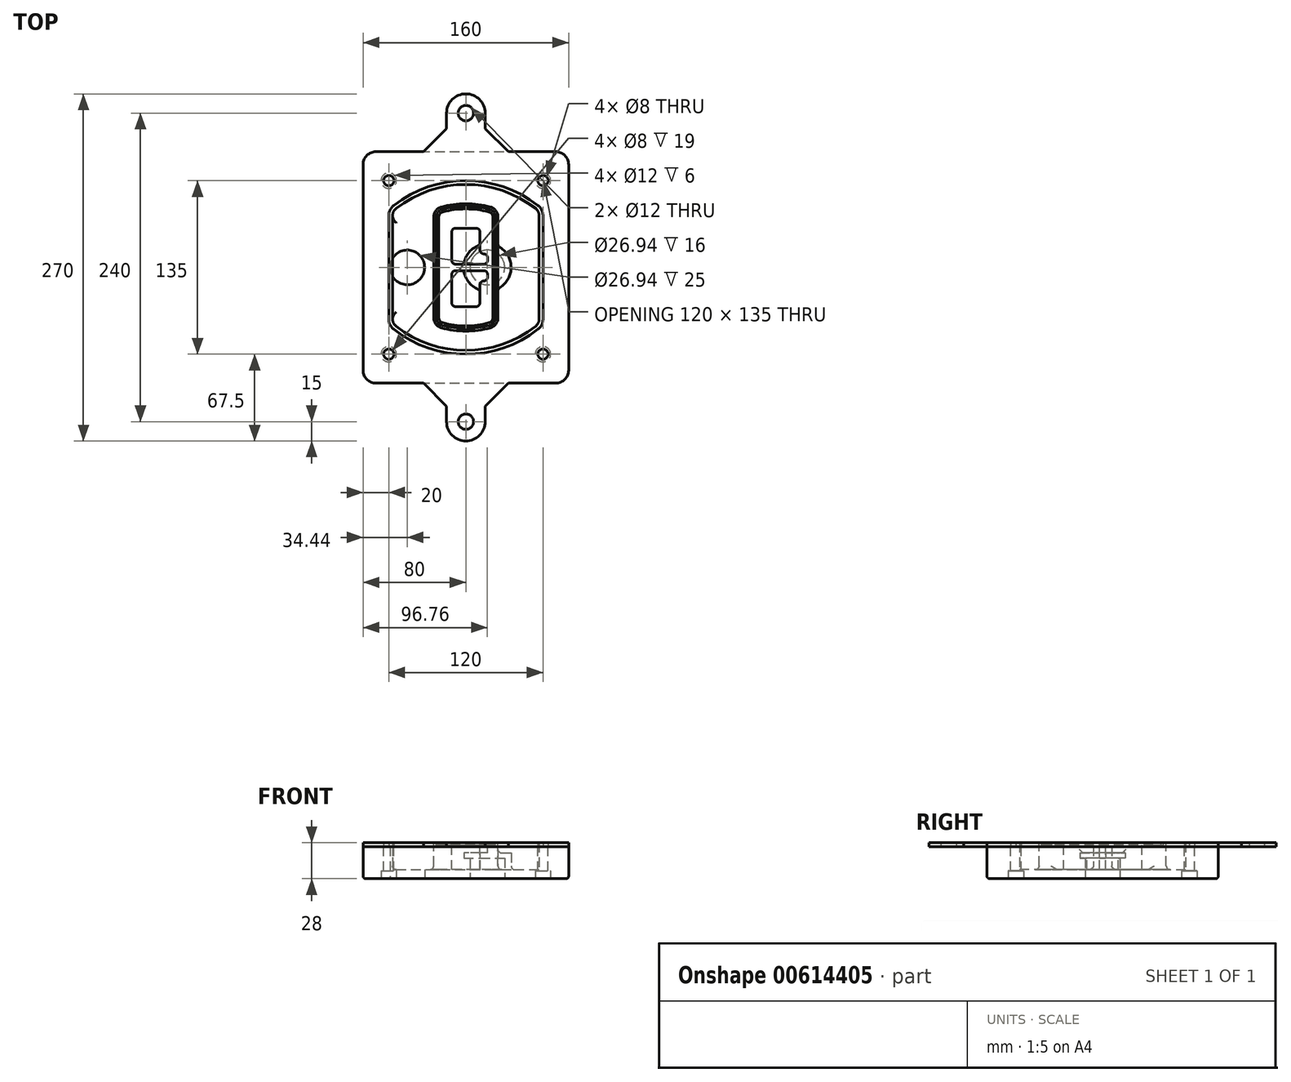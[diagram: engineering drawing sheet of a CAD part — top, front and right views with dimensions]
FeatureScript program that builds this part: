
annotation { "Feature Type Name" : "Feature", "Feature Type Description" : "" }
export const myFeature = defineFeature(function(context is Context, id is Id, definition is map)
    precondition{}
    {
        {
            var Q0;
            Q0=qCreatedBy(makeId("Top.planeOp"),FACE);
            var sketch = newSketch(context, id + "F0", { "sketchPlane" : qUnion([Q0])});
            skPoint(sketch, "E0.rect.middle", {"position": v(0, 0) * mm});
            skLineSegment(sketch, "E1.bottom", {"start": v(-70, -90) * mm, "end": v(70, -90) * mm});
            skLineSegment(sketch, "E1.top", {"start": v(-70, 90) * mm, "end": v(70, 90) * mm});
            skLineSegment(sketch, "E1.left", {"start": v(-80, -80) * mm, "end": v(-80, 80) * mm});
            skLineSegment(sketch, "E1.right", {"start": v(80, -80) * mm, "end": v(80, 80) * mm});
            skLineSegment(sketch, "E2", {"start": v(-80, 90) * mm, "end": v(80, -90) * mm, "construction": true});
            skLineSegment(sketch, "E3", {"start": v(80, 90) * mm, "end": v(-80, -90) * mm, "construction": true});
            skCircle(sketch, "E4", {"center": v(-60, 67.5) * mm, "radius": 4 * mm});
            skCircle(sketch, "E5", {"center": v(60, 67.5) * mm, "radius": 4 * mm});
            skCircle(sketch, "E6", {"center": v(60, -67.5) * mm, "radius": 4 * mm});
            skCircle(sketch, "E7", {"center": v(-60, -67.5) * mm, "radius": 4 * mm});
            skLineSegment(sketch, "E8", {"start": v(-60, 67.5) * mm, "end": v(60, 67.5) * mm, "construction": true});
            skLineSegment(sketch, "E9", {"start": v(60, 67.5) * mm, "end": v(60, -67.5) * mm, "construction": true});
            skLineSegment(sketch, "E10", {"start": v(60, -67.5) * mm, "end": v(-60, -67.5) * mm, "construction": true});
            skLineSegment(sketch, "E11", {"start": v(-60, -67.5) * mm, "end": v(-60, 67.5) * mm, "construction": true});
            skLineSegment(sketch, "E12", {"start": v(-60, 40.3) * mm, "end": v(-60, -40.3) * mm});
            skLineSegment(sketch, "E13", {"start": v(60, 40.3) * mm, "end": v(60, -40.3) * mm});
            skArc(sketch, "E14", {"start": v(56.15, 48.18) * mm, "mid": v(0, 67.5) * mm, "end": v(-56.15, 48.18) * mm});
            skArc(sketch, "E15", {"start": v(-56.15, -48.18) * mm, "mid": v(0, -67.5) * mm, "end": v(56.15, -48.18) * mm});
            skLineSegment(sketch, "E16", {"start": v(-60, 0) * mm, "end": v(60, 0) * mm, "construction": true});
            skPoint(sketch, "E17.visualSharp", {"position": v(-60, -45) * mm});
            skArc(sketch, "E17.filletArc", {"start": v(-60, -40.3) * mm, "mid": v(-58.99, -44.68) * mm, "end": v(-56.15, -48.18) * mm});
            skPoint(sketch, "E18.visualSharp", {"position": v(-60, 45) * mm});
            skArc(sketch, "E18.filletArc", {"start": v(-56.15, 48.18) * mm, "mid": v(-58.99, 44.68) * mm, "end": v(-60, 40.3) * mm});
            skPoint(sketch, "E19.visualSharp", {"position": v(60, 45) * mm});
            skArc(sketch, "E19.filletArc", {"start": v(60, 40.3) * mm, "mid": v(58.99, 44.68) * mm, "end": v(56.15, 48.18) * mm});
            skPoint(sketch, "E20.visualSharp", {"position": v(60, -45) * mm});
            skArc(sketch, "E20.filletArc", {"start": v(56.15, -48.18) * mm, "mid": v(58.99, -44.68) * mm, "end": v(60, -40.3) * mm});
            skPoint(sketch, "E21.visualSharp", {"position": v(-80, 90) * mm});
            skArc(sketch, "E21.filletArc", {"start": v(-70, 90) * mm, "mid": v(-77.07, 87.07) * mm, "end": v(-80, 80) * mm});
            skPoint(sketch, "E22.visualSharp", {"position": v(80, 90) * mm});
            skArc(sketch, "E22.filletArc", {"start": v(80, 80) * mm, "mid": v(77.07, 87.07) * mm, "end": v(70, 90) * mm});
            skPoint(sketch, "E23.visualSharp", {"position": v(80, -90) * mm});
            skArc(sketch, "E23.filletArc", {"start": v(70, -90) * mm, "mid": v(77.07, -87.07) * mm, "end": v(80, -80) * mm});
            skPoint(sketch, "E24.visualSharp", {"position": v(-80, -90) * mm});
            skArc(sketch, "E24.filletArc", {"start": v(-80, -80) * mm, "mid": v(-77.07, -87.07) * mm, "end": v(-70, -90) * mm});
            skArc(sketch, "E25.0", {"start": v(57, 40.3) * mm, "mid": v(56.3, 43.36) * mm, "end": v(54.3, 45.81) * mm});
            skLineSegment(sketch, "E25.1", {"start": v(57, 40.3) * mm, "end": v(57, -40.3) * mm});
            skArc(sketch, "E25.2", {"start": v(54.3, -45.81) * mm, "mid": v(56.3, -43.36) * mm, "end": v(57, -40.3) * mm});
            skArc(sketch, "E25.3", {"start": v(-54.3, -45.81) * mm, "mid": v(0, -64.5) * mm, "end": v(54.3, -45.81) * mm});
            skArc(sketch, "E25.4", {"start": v(-57, -40.3) * mm, "mid": v(-56.3, -43.36) * mm, "end": v(-54.3, -45.81) * mm});
            skArc(sketch, "E25.5", {"start": v(54.3, 45.81) * mm, "mid": v(0, 64.5) * mm, "end": v(-54.3, 45.81) * mm});
            skLineSegment(sketch, "E25.6", {"start": v(-57, 40.3) * mm, "end": v(-57, -40.3) * mm});
            skArc(sketch, "E25.7", {"start": v(-54.3, 45.81) * mm, "mid": v(-56.3, 43.36) * mm, "end": v(-57, 40.3) * mm});
            skArc(sketch, "E26.0", {"start": v(-58.62, 51.33) * mm, "mid": v(-62.58, 46.43) * mm, "end": v(-64, 40.3) * mm});
            skArc(sketch, "E26.1", {"start": v(58.62, 51.33) * mm, "mid": v(0, 71.5) * mm, "end": v(-58.62, 51.33) * mm});
            skArc(sketch, "E26.2", {"start": v(64, 40.3) * mm, "mid": v(62.58, 46.43) * mm, "end": v(58.62, 51.33) * mm});
            skLineSegment(sketch, "E26.3", {"start": v(64, 40.3) * mm, "end": v(64, -40.3) * mm});
            skArc(sketch, "E26.4", {"start": v(58.62, -51.33) * mm, "mid": v(62.58, -46.43) * mm, "end": v(64, -40.3) * mm});
            skLineSegment(sketch, "E26.5", {"start": v(-64, 40.3) * mm, "end": v(-64, -40.3) * mm});
            skArc(sketch, "E26.6", {"start": v(-58.62, -51.33) * mm, "mid": v(0, -71.5) * mm, "end": v(58.62, -51.33) * mm});
            skArc(sketch, "E26.7", {"start": v(-64, -40.3) * mm, "mid": v(-62.58, -46.43) * mm, "end": v(-58.62, -51.33) * mm});
            skSolve(sketch);
        }
        {
            var Q0;
            Q0=makeQuery(id+"F0.imprint","IMPRINT",FACE,{"disambiguationData":[TD([[makeQuery(id+"F0.imprint","IMPRINT",EDGE,{"derivedFrom":sQuery(id+"F0.wireOp",EDGE,"E1.bottom")}),1.0]])]});
            var Q1;
            Q1=makeQuery(id+"F0.imprint","IMPRINT",FACE,{"disambiguationData":[TD([[makeQuery(id+"F0.imprint","IMPRINT",EDGE,{"derivedFrom":sQuery(id+"F0.wireOp",EDGE,"E12")}),1.0]])]});
            var Q2;
            Q2=makeQuery(id+"F0.imprint","IMPRINT",FACE,{"disambiguationData":[TD([[makeQuery(id+"F0.imprint","IMPRINT",EDGE,{"derivedFrom":sQuery(id+"F0.wireOp",EDGE,"E25.0")}),1.0]])]});
            var Q3;
            Q3=makeQuery(id+"F0.imprint","IMPRINT",FACE,{"disambiguationData":[TD([[makeQuery(id+"F0.imprint","IMPRINT",EDGE,{"derivedFrom":sQuery(id+"F0.wireOp",EDGE,"E12")}),-1.0]])]});
            extrude(context, id + "F1", {"entities" : qUnion([Q0, Q1, Q2, Q3]), "oppositeDirection" : true, "depth" : 25 * mm});
        }
        {
            var Q0;
            Q0=makeQuery(id+"F0.imprint","IMPRINT",FACE,{"disambiguationData":[TD([[makeQuery(id+"F0.imprint","IMPRINT",EDGE,{"derivedFrom":sQuery(id+"F0.wireOp",EDGE,"E12")}),1.0]])]});
            extrude(context, id + "F2", {"entities" : qUnion([Q0]), "operationType" : NewBodyOperationType.ADD, "depth" : 3 * mm});
        }
        {
            var Q0;
            Q0=makeQuery(id+"F0.imprint","IMPRINT",FACE,{"disambiguationData":[TD([[makeQuery(id+"F0.imprint","IMPRINT",EDGE,{"derivedFrom":sQuery(id+"F0.wireOp",EDGE,"E25.0")}),1.0]])]});
            extrude(context, id + "F3", {"entities" : qUnion([Q0]), "operationType" : NewBodyOperationType.REMOVE, "oppositeDirection" : true, "depth" : 18 * mm});
        }
        {
            var Q0;
            Q0=makeQuery(id+"F2.opExtrude","CAP_FACE",FACE,{"disambiguationData":[OSD([sQuery(id+"F0.wireOp",EDGE,"E12"),sQuery(id+"F0.wireOp",EDGE,"E13"),sQuery(id+"F0.wireOp",EDGE,"E14"),sQuery(id+"F0.wireOp",EDGE,"E15"),sQuery(id+"F0.wireOp",EDGE,"E17.filletArc"),sQuery(id+"F0.wireOp",EDGE,"E18.filletArc"),sQuery(id+"F0.wireOp",EDGE,"E19.filletArc"),sQuery(id+"F0.wireOp",EDGE,"E20.filletArc"),sQuery(id+"F0.wireOp",EDGE,"E25.0"),sQuery(id+"F0.wireOp",EDGE,"E25.1"),sQuery(id+"F0.wireOp",EDGE,"E25.2"),sQuery(id+"F0.wireOp",EDGE,"E25.3"),sQuery(id+"F0.wireOp",EDGE,"E25.4"),sQuery(id+"F0.wireOp",EDGE,"E25.5"),sQuery(id+"F0.wireOp",EDGE,"E25.6"),sQuery(id+"F0.wireOp",EDGE,"E25.7")])],"isStart":false});
            var sketch = newSketch(context, id + "F4", { "sketchPlane" : qUnion([Q0])});
            skArc(sketch, "E27.0", {"start": v(-19.08, -46.97) * mm, "mid": v(0, -49.5) * mm, "end": v(19.08, -46.97) * mm});
            skArc(sketch, "E28.0", {"start": v(19.08, 46.97) * mm, "mid": v(0, 49.5) * mm, "end": v(-19.08, 46.97) * mm});
            skLineSegment(sketch, "E29", {"start": v(-25, 39.25) * mm, "end": v(-25, -39.25) * mm});
            skLineSegment(sketch, "E30", {"start": v(25, 39.25) * mm, "end": v(25, -39.25) * mm});
            skLineSegment(sketch, "E31", {"start": v(-25, 45.1) * mm, "end": v(25, 45.1) * mm, "construction": true});
            skLineSegment(sketch, "E32", {"start": v(-25, -45.1) * mm, "end": v(25, -45.1) * mm, "construction": true});
            skPoint(sketch, "E33.visualSharp", {"position": v(-25, 45.1) * mm});
            skArc(sketch, "E33.filletArc", {"start": v(-19.08, 46.97) * mm, "mid": v(-23.35, 44.11) * mm, "end": v(-25, 39.25) * mm});
            skPoint(sketch, "E34.visualSharp", {"position": v(25, 45.1) * mm});
            skArc(sketch, "E34.filletArc", {"start": v(25, 39.25) * mm, "mid": v(23.35, 44.11) * mm, "end": v(19.08, 46.97) * mm});
            skPoint(sketch, "E35.visualSharp", {"position": v(25, -45.1) * mm});
            skArc(sketch, "E35.filletArc", {"start": v(19.08, -46.97) * mm, "mid": v(23.35, -44.11) * mm, "end": v(25, -39.25) * mm});
            skPoint(sketch, "E36.visualSharp", {"position": v(-25, -45.1) * mm});
            skArc(sketch, "E36.filletArc", {"start": v(-25, -39.25) * mm, "mid": v(-23.35, -44.11) * mm, "end": v(-19.08, -46.97) * mm});
            skArc(sketch, "E37.0", {"start": v(54.3, 45.81) * mm, "mid": v(0, 64.5) * mm, "end": v(-54.3, 45.81) * mm});
            skArc(sketch, "E37.1", {"start": v(-54.3, 45.81) * mm, "mid": v(-56.3, 43.36) * mm, "end": v(-57, 40.3) * mm});
            skLineSegment(sketch, "E37.2", {"start": v(-57, 40.3) * mm, "end": v(-57, -40.3) * mm});
            skArc(sketch, "E37.3", {"start": v(-57, -40.3) * mm, "mid": v(-56.3, -43.36) * mm, "end": v(-54.3, -45.81) * mm});
            skArc(sketch, "E37.4", {"start": v(-54.3, -45.81) * mm, "mid": v(0, -64.5) * mm, "end": v(54.3, -45.81) * mm});
            skArc(sketch, "E37.5", {"start": v(54.3, -45.81) * mm, "mid": v(56.3, -43.36) * mm, "end": v(57, -40.3) * mm});
            skLineSegment(sketch, "E37.6", {"start": v(57, 40.3) * mm, "end": v(57, -40.3) * mm});
            skArc(sketch, "E37.7", {"start": v(57, 40.3) * mm, "mid": v(56.3, 43.36) * mm, "end": v(54.3, 45.81) * mm});
            skLineSegment(sketch, "E38.0", {"start": v(23, 39.25) * mm, "end": v(23, -39.25) * mm});
            skArc(sketch, "E38.1", {"start": v(18.56, -45.04) * mm, "mid": v(21.76, -42.9) * mm, "end": v(23, -39.25) * mm});
            skArc(sketch, "E38.2", {"start": v(-18.56, -45.04) * mm, "mid": v(0, -47.5) * mm, "end": v(18.56, -45.04) * mm});
            skArc(sketch, "E38.3", {"start": v(-23, -39.25) * mm, "mid": v(-21.76, -42.9) * mm, "end": v(-18.56, -45.04) * mm});
            skLineSegment(sketch, "E38.4", {"start": v(-23, 39.25) * mm, "end": v(-23, -39.25) * mm});
            skArc(sketch, "E38.5", {"start": v(23, 39.25) * mm, "mid": v(21.76, 42.9) * mm, "end": v(18.56, 45.04) * mm});
            skArc(sketch, "E38.6", {"start": v(-18.56, 45.04) * mm, "mid": v(-21.76, 42.9) * mm, "end": v(-23, 39.25) * mm});
            skArc(sketch, "E38.7", {"start": v(18.56, 45.04) * mm, "mid": v(0, 47.5) * mm, "end": v(-18.56, 45.04) * mm});
            skArc(sketch, "E39.0", {"start": v(21, 39.25) * mm, "mid": v(20.18, 41.68) * mm, "end": v(18.04, 43.1) * mm});
            skLineSegment(sketch, "E39.1", {"start": v(21, 39.25) * mm, "end": v(21, -39.25) * mm});
            skArc(sketch, "E39.2", {"start": v(18.04, -43.1) * mm, "mid": v(20.18, -41.68) * mm, "end": v(21, -39.25) * mm});
            skArc(sketch, "E39.3", {"start": v(-18.04, -43.1) * mm, "mid": v(0, -45.5) * mm, "end": v(18.04, -43.1) * mm});
            skArc(sketch, "E39.4", {"start": v(-21, -39.25) * mm, "mid": v(-20.18, -41.68) * mm, "end": v(-18.04, -43.1) * mm});
            skArc(sketch, "E39.5", {"start": v(18.04, 43.1) * mm, "mid": v(0, 45.5) * mm, "end": v(-18.04, 43.1) * mm});
            skLineSegment(sketch, "E39.6", {"start": v(-21, 39.25) * mm, "end": v(-21, -39.25) * mm});
            skArc(sketch, "E39.7", {"start": v(-18.04, 43.1) * mm, "mid": v(-20.18, 41.68) * mm, "end": v(-21, 39.25) * mm});
            skLineSegment(sketch, "E40", {"start": v(-25, 0) * mm, "end": v(25, 0) * mm, "construction": true});
            skLineSegment(sketch, "E41", {"start": v(-11, 5.5) * mm, "end": v(-11, 27.5) * mm});
            skLineSegment(sketch, "E42", {"start": v(-8, 30.5) * mm, "end": v(8, 30.5) * mm});
            skLineSegment(sketch, "E43", {"start": v(11, 27.5) * mm, "end": v(11, 13.5) * mm});
            skLineSegment(sketch, "E44", {"start": v(14, 10.5) * mm, "end": v(14, 10.5) * mm});
            skLineSegment(sketch, "E45", {"start": v(17, 7.5) * mm, "end": v(17, 5.5) * mm});
            skLineSegment(sketch, "E46", {"start": v(14, 2.5) * mm, "end": v(-8, 2.5) * mm});
            skPoint(sketch, "E47.visualSharp", {"position": v(-11, 30.5) * mm});
            skArc(sketch, "E47.filletArc", {"start": v(-8, 30.5) * mm, "mid": v(-10.12, 29.62) * mm, "end": v(-11, 27.5) * mm});
            skPoint(sketch, "E48.visualSharp", {"position": v(11, 30.5) * mm});
            skArc(sketch, "E48.filletArc", {"start": v(11, 27.5) * mm, "mid": v(10.12, 29.62) * mm, "end": v(8, 30.5) * mm});
            skPoint(sketch, "E49.visualSharp", {"position": v(11, 10.5) * mm});
            skArc(sketch, "E49.filletArc", {"start": v(11, 13.5) * mm, "mid": v(11.88, 11.38) * mm, "end": v(14, 10.5) * mm});
            skPoint(sketch, "E50.visualSharp", {"position": v(17, 10.5) * mm});
            skArc(sketch, "E50.filletArc", {"start": v(17, 7.5) * mm, "mid": v(16.12, 9.62) * mm, "end": v(14, 10.5) * mm});
            skPoint(sketch, "E51.visualSharp", {"position": v(17, 2.5) * mm});
            skArc(sketch, "E51.filletArc", {"start": v(14, 2.5) * mm, "mid": v(16.12, 3.38) * mm, "end": v(17, 5.5) * mm});
            skPoint(sketch, "E52.visualSharp", {"position": v(-11, 2.5) * mm});
            skArc(sketch, "E52.filletArc", {"start": v(-11, 5.5) * mm, "mid": v(-10.12, 3.38) * mm, "end": v(-8, 2.5) * mm});
            skLineSegment(sketch, "E53.0.MirrorCS", {"start": v(14, -2.5) * mm, "end": v(-8, -2.5) * mm});
            skArc(sketch, "E54.0.MirrorCS", {"start": v(-11, -5.5) * mm, "mid": v(-10.12, -3.38) * mm, "end": v(-8, -2.5) * mm});
            skLineSegment(sketch, "E55.0.MirrorCS", {"start": v(-11, -5.5) * mm, "end": v(-11, -27.5) * mm});
            skArc(sketch, "E56.0.MirrorCS", {"start": v(-8, -30.5) * mm, "mid": v(-10.12, -29.62) * mm, "end": v(-11, -27.5) * mm});
            skLineSegment(sketch, "E57.0.MirrorCS", {"start": v(-8, -30.5) * mm, "end": v(8, -30.5) * mm});
            skArc(sketch, "E58.0.MirrorCS", {"start": v(11, -27.5) * mm, "mid": v(10.12, -29.62) * mm, "end": v(8, -30.5) * mm});
            skLineSegment(sketch, "E59.0.MirrorCS", {"start": v(11, -27.5) * mm, "end": v(11, -13.5) * mm});
            skArc(sketch, "E60.0.MirrorCS", {"start": v(11, -13.5) * mm, "mid": v(11.88, -11.38) * mm, "end": v(14, -10.5) * mm});
            skArc(sketch, "E61.0.MirrorCS", {"start": v(17, -7.5) * mm, "mid": v(16.12, -9.62) * mm, "end": v(14, -10.5) * mm});
            skLineSegment(sketch, "E62.0.MirrorCS", {"start": v(17, -7.5) * mm, "end": v(17, -5.5) * mm});
            skArc(sketch, "E63.0.MirrorCS", {"start": v(14, -2.5) * mm, "mid": v(16.12, -3.38) * mm, "end": v(17, -5.5) * mm});
            skSolve(sketch);
        }
        {
            var Q0;
            Q0=makeQuery(id+"F4.imprint","IMPRINT",FACE,{"disambiguationData":[TD([[makeQuery(id+"F4.imprint","IMPRINT",EDGE,{"derivedFrom":sQuery(id+"F4.wireOp",EDGE,"E27.0")}),1.0]])]});
            var Q1;
            Q1=makeQuery(id+"F4.imprint","IMPRINT",FACE,{"disambiguationData":[TD([[makeQuery(id+"F4.imprint","IMPRINT",EDGE,{"derivedFrom":sQuery(id+"F4.wireOp",EDGE,"E38.0")}),-1.0]])]});
            var Q2;
            Q2=makeQuery(id+"F4.imprint","IMPRINT",FACE,{"disambiguationData":[TD([[makeQuery(id+"F4.imprint","IMPRINT",EDGE,{"derivedFrom":sQuery(id+"F4.wireOp",EDGE,"E39.0")}),1.0]])]});
            extrude(context, id + "F5", {"entities" : qUnion([Q0, Q1, Q2]), "operationType" : NewBodyOperationType.ADD, "endBound" : BoundingType.UP_TO_NEXT, "oppositeDirection" : true, "depth" : 25 * mm});
        }
        {
            var Q0;
            Q0=makeQuery(id+"F4.imprint","IMPRINT",FACE,{"disambiguationData":[TD([[makeQuery(id+"F4.imprint","IMPRINT",EDGE,{"derivedFrom":sQuery(id+"F4.wireOp",EDGE,"E38.0")}),-1.0]])]});
            extrude(context, id + "F6", {"entities" : qUnion([Q0]), "operationType" : NewBodyOperationType.REMOVE, "oppositeDirection" : true, "depth" : 2 * mm});
        }
        {
            var Q0;
            Q0=makeQuery(id+"F1.opExtrude","CAP_FACE",FACE,{"disambiguationData":[OSD([sQuery(id+"F0.wireOp",EDGE,"E1.bottom"),sQuery(id+"F0.wireOp",EDGE,"E1.top"),sQuery(id+"F0.wireOp",EDGE,"E1.left"),sQuery(id+"F0.wireOp",EDGE,"E1.right"),sQuery(id+"F0.wireOp",EDGE,"E4"),sQuery(id+"F0.wireOp",EDGE,"E5"),sQuery(id+"F0.wireOp",EDGE,"E6"),sQuery(id+"F0.wireOp",EDGE,"E7"),sQuery(id+"F0.wireOp",EDGE,"E21.filletArc"),sQuery(id+"F0.wireOp",EDGE,"E22.filletArc"),sQuery(id+"F0.wireOp",EDGE,"E23.filletArc"),sQuery(id+"F0.wireOp",EDGE,"E24.filletArc")])],"isStart":false});
            var sketch = newSketch(context, id + "F7", { "sketchPlane" : qUnion([Q0])});
            skCircle(sketch, "E64", {"center": v(16.76, 0) * mm, "radius": 13.47 * mm});
            skCircle(sketch, "E65", {"center": v(-45.56, 0) * mm, "radius": 13.47 * mm});
            skLineSegment(sketch, "E66", {"start": v(80, 0) * mm, "end": v(-80, 0) * mm});
            skCircle(sketch, "E67", {"center": v(16.76, 0) * mm, "radius": 18.47 * mm});
            skCircle(sketch, "E68", {"center": v(60, -67.5) * mm, "radius": 6 * mm});
            skCircle(sketch, "E69", {"center": v(-60, -67.5) * mm, "radius": 6 * mm});
            skCircle(sketch, "E70", {"center": v(-60, 67.5) * mm, "radius": 6 * mm});
            skCircle(sketch, "E71", {"center": v(60, 67.5) * mm, "radius": 6 * mm});
            skSolve(sketch);
        }
        {
            var Q0;
            {var subQ1=sQuery(id+"F7.wireOp",EDGE,"E66");var subQ4=sQuery(id+"F7.wireOp",EDGE,"E64");var subQ6=makeQuery(id+"F7.imprint","INTERSECT",VERTEX,{"disambiguationData":[OD(0.0)],"derivedFrom":[subQ4,subQ1]});Q0=makeQuery(id+"F7.imprint","IMPRINT",FACE,{"disambiguationData":[TD([[makeQuery(id+"F7.imprint","IMPRINT",EDGE,{"disambiguationData":[TD([[subQ6,-1.0]])],"derivedFrom":subQ4}),-1.0]])]});}
            var Q1;
            {var subQ0=sQuery(id+"F7.wireOp",EDGE,"E66");var subQ1=sQuery(id+"F7.wireOp",EDGE,"E64");var subQ3=makeQuery(id+"F7.imprint","INTERSECT",VERTEX,{"disambiguationData":[OD(0.0)],"derivedFrom":[subQ1,subQ0]});Q1=makeQuery(id+"F7.imprint","IMPRINT",FACE,{"disambiguationData":[TD([[makeQuery(id+"F7.imprint","IMPRINT",EDGE,{"disambiguationData":[TD([[subQ3,-1.0]])],"derivedFrom":subQ1}),1.0]])]});}
            var Q2;
            {var subQ0=sQuery(id+"F7.wireOp",EDGE,"E66");var subQ1=sQuery(id+"F7.wireOp",EDGE,"E64");var subQ3=makeQuery(id+"F7.imprint","INTERSECT",VERTEX,{"disambiguationData":[OD(0.0)],"derivedFrom":[subQ1,subQ0]});Q2=makeQuery(id+"F7.imprint","IMPRINT",FACE,{"disambiguationData":[TD([[makeQuery(id+"F7.imprint","IMPRINT",EDGE,{"disambiguationData":[TD([[subQ3,1.0]])],"derivedFrom":subQ1}),1.0]])]});}
            var Q3;
            {var subQ1=sQuery(id+"F7.wireOp",EDGE,"E66");var subQ4=sQuery(id+"F7.wireOp",EDGE,"E64");var subQ6=makeQuery(id+"F7.imprint","INTERSECT",VERTEX,{"disambiguationData":[OD(0.0)],"derivedFrom":[subQ4,subQ1]});Q3=makeQuery(id+"F7.imprint","IMPRINT",FACE,{"disambiguationData":[TD([[makeQuery(id+"F7.imprint","IMPRINT",EDGE,{"disambiguationData":[TD([[subQ6,1.0]])],"derivedFrom":subQ4}),-1.0]])]});}
            extrude(context, id + "F8", {"entities" : qUnion([Q0, Q1, Q2, Q3]), "operationType" : NewBodyOperationType.ADD, "oppositeDirection" : true, "depth" : 20 * mm});
        }
        {
            var Q0;
            {var subQ0=sQuery(id+"F7.wireOp",EDGE,"E66");var subQ1=sQuery(id+"F7.wireOp",EDGE,"E64");var subQ3=makeQuery(id+"F7.imprint","INTERSECT",VERTEX,{"disambiguationData":[OD(0.0)],"derivedFrom":[subQ1,subQ0]});Q0=makeQuery(id+"F7.imprint","IMPRINT",FACE,{"disambiguationData":[TD([[makeQuery(id+"F7.imprint","IMPRINT",EDGE,{"disambiguationData":[TD([[subQ3,-1.0]])],"derivedFrom":subQ1}),1.0]])]});}
            var Q1;
            {var subQ0=sQuery(id+"F7.wireOp",EDGE,"E66");var subQ1=sQuery(id+"F7.wireOp",EDGE,"E64");var subQ3=makeQuery(id+"F7.imprint","INTERSECT",VERTEX,{"disambiguationData":[OD(0.0)],"derivedFrom":[subQ1,subQ0]});Q1=makeQuery(id+"F7.imprint","IMPRINT",FACE,{"disambiguationData":[TD([[makeQuery(id+"F7.imprint","IMPRINT",EDGE,{"disambiguationData":[TD([[subQ3,1.0]])],"derivedFrom":subQ1}),1.0]])]});}
            extrude(context, id + "F9", {"entities" : qUnion([Q0, Q1]), "operationType" : NewBodyOperationType.REMOVE, "oppositeDirection" : true, "depth" : 16 * mm});
        }
        {
            var Q0;
            {var subQ0=sQuery(id+"F7.wireOp",EDGE,"E66");var subQ1=sQuery(id+"F7.wireOp",EDGE,"E65");var subQ3=makeQuery(id+"F7.imprint","INTERSECT",VERTEX,{"disambiguationData":[OD(0.0)],"derivedFrom":[subQ1,subQ0]});Q0=makeQuery(id+"F7.imprint","IMPRINT",FACE,{"disambiguationData":[TD([[makeQuery(id+"F7.imprint","IMPRINT",EDGE,{"disambiguationData":[TD([[subQ3,-1.0]])],"derivedFrom":subQ1}),1.0]])]});}
            var Q1;
            {var subQ0=sQuery(id+"F7.wireOp",EDGE,"E66");var subQ1=sQuery(id+"F7.wireOp",EDGE,"E65");var subQ3=makeQuery(id+"F7.imprint","INTERSECT",VERTEX,{"disambiguationData":[OD(0.0)],"derivedFrom":[subQ1,subQ0]});Q1=makeQuery(id+"F7.imprint","IMPRINT",FACE,{"disambiguationData":[TD([[makeQuery(id+"F7.imprint","IMPRINT",EDGE,{"disambiguationData":[TD([[subQ3,1.0]])],"derivedFrom":subQ1}),1.0]])]});}
            extrude(context, id + "F10", {"entities" : qUnion([Q0, Q1]), "operationType" : NewBodyOperationType.REMOVE, "oppositeDirection" : true, "depth" : 25 * mm});
        }
        {
            var Q0;
            Q0=makeQuery(id+"F7.imprint","IMPRINT",FACE,{"disambiguationData":[TD([[makeQuery(id+"F7.imprint","IMPRINT",EDGE,{"derivedFrom":sQuery(id+"F7.wireOp",EDGE,"E68")}),1.0]])]});
            var Q1;
            Q1=makeQuery(id+"F7.imprint","IMPRINT",FACE,{"disambiguationData":[TD([[makeQuery(id+"F7.imprint","IMPRINT",EDGE,{"derivedFrom":makeQuery(id+"F1.opExtrude","CAP_EDGE",EDGE,{"disambiguationData":[OSD([sQuery(id+"F0.wireOp",EDGE,"E5")])],"isStart":false})}),-1.0]])]});
            var Q2;
            Q2=makeQuery(id+"F7.imprint","IMPRINT",FACE,{"disambiguationData":[TD([[makeQuery(id+"F7.imprint","IMPRINT",EDGE,{"derivedFrom":sQuery(id+"F7.wireOp",EDGE,"E69")}),1.0]])]});
            var Q3;
            Q3=makeQuery(id+"F7.imprint","IMPRINT",FACE,{"disambiguationData":[TD([[makeQuery(id+"F7.imprint","IMPRINT",EDGE,{"derivedFrom":makeQuery(id+"F1.opExtrude","CAP_EDGE",EDGE,{"disambiguationData":[OSD([sQuery(id+"F0.wireOp",EDGE,"E4")])],"isStart":false})}),-1.0]])]});
            var Q4;
            Q4=makeQuery(id+"F7.imprint","IMPRINT",FACE,{"disambiguationData":[TD([[makeQuery(id+"F7.imprint","IMPRINT",EDGE,{"derivedFrom":sQuery(id+"F7.wireOp",EDGE,"E70")}),1.0]])]});
            var Q5;
            Q5=makeQuery(id+"F7.imprint","IMPRINT",FACE,{"disambiguationData":[TD([[makeQuery(id+"F7.imprint","IMPRINT",EDGE,{"derivedFrom":makeQuery(id+"F1.opExtrude","CAP_EDGE",EDGE,{"disambiguationData":[OSD([sQuery(id+"F0.wireOp",EDGE,"E7")])],"isStart":false})}),-1.0]])]});
            var Q6;
            Q6=makeQuery(id+"F7.imprint","IMPRINT",FACE,{"disambiguationData":[TD([[makeQuery(id+"F7.imprint","IMPRINT",EDGE,{"derivedFrom":sQuery(id+"F7.wireOp",EDGE,"E71")}),1.0]])]});
            var Q7;
            Q7=makeQuery(id+"F7.imprint","IMPRINT",FACE,{"disambiguationData":[TD([[makeQuery(id+"F7.imprint","IMPRINT",EDGE,{"derivedFrom":makeQuery(id+"F1.opExtrude","CAP_EDGE",EDGE,{"disambiguationData":[OSD([sQuery(id+"F0.wireOp",EDGE,"E6")])],"isStart":false})}),-1.0]])]});
            extrude(context, id + "F11", {"entities" : qUnion([Q0, Q1, Q2, Q3, Q4, Q5, Q6, Q7]), "operationType" : NewBodyOperationType.REMOVE, "oppositeDirection" : true, "depth" : 6 * mm});
        }
        {
            var Q0;
            Q0=makeQuery(id+"F9.boolean.opBoolean","COPY",FACE,{"derivedFrom":makeQuery(id+"F9.opExtrude","CAP_FACE",FACE,{"disambiguationData":[OSD([sQuery(id+"F7.wireOp",EDGE,"E64")])],"isStart":false})});
            var sketch = newSketch(context, id + "F12", { "sketchPlane" : qUnion([Q0])});
            skArc(sketch, "E72.0", {"start": v(11, 17.55) * mm, "mid": v(2.57, 11.82) * mm, "end": v(-1.54, 2.5) * mm});
            skArc(sketch, "E72.1", {"start": v(-1.54, -2.5) * mm, "mid": v(2.57, -11.82) * mm, "end": v(11, -17.55) * mm});
            skLineSegment(sketch, "E73", {"start": v(-1.54, -2.5) * mm, "end": v(14, -2.5) * mm});
            skLineSegment(sketch, "E74.0", {"start": v(14, 2.5) * mm, "end": v(-1.54, 2.5) * mm});
            skArc(sketch, "E74.1", {"start": v(14, 2.5) * mm, "mid": v(16.12, 3.38) * mm, "end": v(17, 5.5) * mm});
            skLineSegment(sketch, "E74.2", {"start": v(17, 7.5) * mm, "end": v(17, 5.5) * mm});
            skArc(sketch, "E74.3", {"start": v(17, 7.5) * mm, "mid": v(16.12, 9.62) * mm, "end": v(14, 10.5) * mm});
            skArc(sketch, "E74.4", {"start": v(11, 13.5) * mm, "mid": v(11.88, 11.38) * mm, "end": v(14, 10.5) * mm});
            skLineSegment(sketch, "E74.5", {"start": v(11, 17.55) * mm, "end": v(11, 13.5) * mm});
            skLineSegment(sketch, "E74.7", {"start": v(14, -2.5) * mm, "end": v(-1.54, -2.5) * mm});
            skArc(sketch, "E74.8", {"start": v(14, -2.5) * mm, "mid": v(16.12, -3.38) * mm, "end": v(17, -5.5) * mm});
            skLineSegment(sketch, "E74.9", {"start": v(17, -7.5) * mm, "end": v(17, -5.5) * mm});
            skArc(sketch, "E74.10", {"start": v(17, -7.5) * mm, "mid": v(16.12, -9.62) * mm, "end": v(14, -10.5) * mm});
            skArc(sketch, "E74.11", {"start": v(11, -13.5) * mm, "mid": v(11.88, -11.38) * mm, "end": v(14, -10.5) * mm});
            skLineSegment(sketch, "E74.12", {"start": v(11, -17.55) * mm, "end": v(11, -13.5) * mm});
            skPoint(sketch, "E75.orphan", {"position": v(11, -27.5) * mm});
            skPoint(sketch, "E76.orphan", {"position": v(-8, -2.5) * mm});
            skPoint(sketch, "E77.orphan", {"position": v(-8, 2.5) * mm});
            skPoint(sketch, "E78.orphan", {"position": v(11, 27.5) * mm});
            skSolve(sketch);
        }
        {
            var Q0;
            {var subQ7=sQuery(id+"F12.wireOp",EDGE,"E72.0");var subQ14=sQuery(id+"F12.wireOp",EDGE,"E72.1");var subQ16=sQuery(id+"F12.wireOp",EDGE,"E74.1");var subQ18=sQuery(id+"F12.wireOp",EDGE,"E74.8");Q0=qUnion([makeQuery(id+"F12.imprint","IMPRINT",FACE,{"disambiguationData":[TD([[makeQuery(id+"F12.imprint","IMPRINT",EDGE,{"derivedFrom":subQ7}),1.0]])]}),makeQuery(id+"F12.imprint","IMPRINT",FACE,{"disambiguationData":[TD([[makeQuery(id+"F12.imprint","IMPRINT",EDGE,{"derivedFrom":subQ14}),1.0]])]}),makeQuery(id+"F12.imprint","IMPRINT",FACE,{"disambiguationData":[TD([[makeQuery(id+"F12.imprint","IMPRINT",EDGE,{"derivedFrom":subQ16}),1.0]])]}),makeQuery(id+"F12.imprint","IMPRINT",FACE,{"disambiguationData":[TD([[makeQuery(id+"F12.imprint","IMPRINT",EDGE,{"derivedFrom":subQ18}),-1.0]])]})]);}
            var Q1;
            Q1=makeQuery(id+"F5.boolean.opBoolean","SPLIT",FACE,{"disambiguationData":[TD([makeQuery(id+"F5.opExtrude","SWEPT_FACE",FACE,{"disambiguationData":[OSD([sQuery(id+"F4.wireOp",EDGE,"E41")])]})])],"derivedFrom":makeQuery(id+"F3.boolean.opBoolean","COPY",FACE,{"derivedFrom":makeQuery(id+"F3.opExtrude","CAP_FACE",FACE,{"disambiguationData":[OSD([sQuery(id+"F0.wireOp",EDGE,"E25.0"),sQuery(id+"F0.wireOp",EDGE,"E25.1"),sQuery(id+"F0.wireOp",EDGE,"E25.2"),sQuery(id+"F0.wireOp",EDGE,"E25.3"),sQuery(id+"F0.wireOp",EDGE,"E25.4"),sQuery(id+"F0.wireOp",EDGE,"E25.5"),sQuery(id+"F0.wireOp",EDGE,"E25.6"),sQuery(id+"F0.wireOp",EDGE,"E25.7")])],"isStart":false})})});
            extrude(context, id + "F13", {"entities" : qUnion([Q0]), "operationType" : NewBodyOperationType.REMOVE, "endBound" : BoundingType.UP_TO_SURFACE, "endBoundEntityFace" : qUnion([Q1]), "depth" : 25 * mm});
        }
        {
            var Q0;
            Q0=makeQuery(id+"F3.boolean.opBoolean","COPY",EDGE,{"derivedFrom":makeQuery(id+"F3.opExtrude","CAP_EDGE",EDGE,{"disambiguationData":[OSD([sQuery(id+"F0.wireOp",EDGE,"E25.6")])],"isStart":false})});
            var Q1;
            Q1=makeQuery(id+"F8.boolean.opBoolean","INTERSECT",EDGE,{"derivedFrom":[makeQuery(id+"F5.opExtrude","SWEPT_FACE",FACE,{"disambiguationData":[OSD([sQuery(id+"F4.wireOp",EDGE,"E30")])]}),makeQuery(id+"F8.opExtrude","CAP_FACE",FACE,{"disambiguationData":[OSD([sQuery(id+"F7.wireOp",EDGE,"E67")])],"isStart":false})]});
            var Q2;
            Q2=makeQuery(id+"F8.boolean.opBoolean","INTERSECT",EDGE,{"disambiguationData":[OD(1.0)],"derivedFrom":[makeQuery(id+"F5.opExtrude","SWEPT_FACE",FACE,{"disambiguationData":[OSD([sQuery(id+"F4.wireOp",EDGE,"E30")])]}),makeQuery(id+"F8.opExtrude","SWEPT_FACE",FACE,{"disambiguationData":[OSD([sQuery(id+"F7.wireOp",EDGE,"E67")])]})]});
            var Q3;
            {var subQ0=sQuery(id+"F4.wireOp",EDGE,"E30");Q3=makeQuery(id+"F8.boolean.opBoolean","SPLIT",EDGE,{"disambiguationData":[TD([makeQuery(id+"F5.opExtrude","SWEPT_FACE",FACE,{"disambiguationData":[OSD([sQuery(id+"F4.wireOp",EDGE,"E35.filletArc")])]})])],"derivedFrom":makeQuery(id+"F5.opExtrude","CAP_EDGE",EDGE,{"disambiguationData":[OSD([subQ0])],"isStart":false})});}
            var Q4;
            {var subQ0=sQuery(id+"F0.wireOp",EDGE,"E25.7");var subQ1=sQuery(id+"F0.wireOp",EDGE,"E25.1");var subQ2=sQuery(id+"F0.wireOp",EDGE,"E25.6");var subQ3=sQuery(id+"F0.wireOp",EDGE,"E25.5");var subQ4=sQuery(id+"F0.wireOp",EDGE,"E25.4");var subQ5=sQuery(id+"F0.wireOp",EDGE,"E25.0");var subQ6=sQuery(id+"F0.wireOp",EDGE,"E25.2");var subQ7=sQuery(id+"F0.wireOp",EDGE,"E25.3");Q4=makeQuery(id+"F8.boolean.opBoolean","INTERSECT",EDGE,{"derivedFrom":[makeQuery(id+"F5.boolean.opBoolean","SPLIT",FACE,{"disambiguationData":[TD([makeQuery(id+"F2.opExtrude","SWEPT_FACE",FACE,{"disambiguationData":[OSD([subQ5])]})])],"derivedFrom":makeQuery(id+"F3.boolean.opBoolean","COPY",FACE,{"derivedFrom":makeQuery(id+"F3.opExtrude","CAP_FACE",FACE,{"disambiguationData":[OSD([subQ5,subQ1,subQ6,subQ7,subQ4,subQ3,subQ2,subQ0])],"isStart":false})})}),makeQuery(id+"F8.opExtrude","SWEPT_FACE",FACE,{"disambiguationData":[OSD([sQuery(id+"F7.wireOp",EDGE,"E67")])]})]});}
            var Q5;
            Q5=makeQuery(id+"F8.boolean.opBoolean","INTERSECT",EDGE,{"disambiguationData":[OD(0.0)],"derivedFrom":[makeQuery(id+"F5.opExtrude","SWEPT_FACE",FACE,{"disambiguationData":[OSD([sQuery(id+"F4.wireOp",EDGE,"E30")])]}),makeQuery(id+"F8.opExtrude","SWEPT_FACE",FACE,{"disambiguationData":[OSD([sQuery(id+"F7.wireOp",EDGE,"E67")])]})]});
            fillet(context, id + "F14", {"entities" : qUnion([Q0, Q1, Q2, Q3, Q4, Q5]), "radius" : 3 * mm, "tangentPropagation" : true, "allowEdgeOverflow" : false});
        }
        {
            var Q0;
            Q0=makeQuery(id+"F1.opExtrude","CAP_EDGE",EDGE,{"disambiguationData":[OSD([sQuery(id+"F0.wireOp",EDGE,"E1.bottom")])],"isStart":false});
            fillet(context, id + "F15", {"entities" : qUnion([Q0]), "radius" : 2 * mm, "tangentPropagation" : true, "allowEdgeOverflow" : false});
        }
        {
            var Q0;
            {var subQ0=sQuery(id+"F0.wireOp",EDGE,"E21.filletArc");var subQ1=sQuery(id+"F0.wireOp",EDGE,"E7");var subQ2=sQuery(id+"F0.wireOp",EDGE,"E6");var subQ3=sQuery(id+"F0.wireOp",EDGE,"E5");var subQ4=sQuery(id+"F0.wireOp",EDGE,"E4");var subQ5=sQuery(id+"F0.wireOp",EDGE,"E22.filletArc");var subQ6=sQuery(id+"F0.wireOp",EDGE,"E1.bottom");var subQ7=sQuery(id+"F0.wireOp",EDGE,"E1.right");var subQ8=sQuery(id+"F0.wireOp",EDGE,"E1.top");var subQ9=sQuery(id+"F0.wireOp",EDGE,"E1.left");var subQ10=sQuery(id+"F0.wireOp",EDGE,"E23.filletArc");var subQ11=sQuery(id+"F0.wireOp",EDGE,"E24.filletArc");Q0=makeQuery(id+"F2.boolean.opBoolean","SPLIT",FACE,{"disambiguationData":[TD([makeQuery(id+"F1.opExtrude","SWEPT_FACE",FACE,{"disambiguationData":[OSD([subQ6])]})])],"derivedFrom":makeQuery(id+"F1.opExtrude","CAP_FACE",FACE,{"disambiguationData":[OSD([subQ6,subQ8,subQ9,subQ7,subQ4,subQ3,subQ2,subQ1,subQ0,subQ5,subQ10,subQ11])],"isStart":true})});}
            var sketch = newSketch(context, id + "F16", { "sketchPlane" : qUnion([Q0])});
            skLineSegment(sketch, "E79", {"start": v(0, 90) * mm, "end": v(0, 120) * mm, "construction": true});
            skCircle(sketch, "E80", {"center": v(0, 120) * mm, "radius": 6 * mm});
            skArc(sketch, "E81", {"start": v(15, 120) * mm, "mid": v(0, 135) * mm, "end": v(-15, 120) * mm});
            skLineSegment(sketch, "E82", {"start": v(-15, 120) * mm, "end": v(-15, 108) * mm});
            skLineSegment(sketch, "E83", {"start": v(-15, 108) * mm, "end": v(-33, 90) * mm});
            skLineSegment(sketch, "E84", {"start": v(15, 120) * mm, "end": v(15, 108) * mm});
            skLineSegment(sketch, "E85", {"start": v(-33, 90) * mm, "end": v(33, 90) * mm});
            skLineSegment(sketch, "E86.MirrorCS", {"start": v(15, 108) * mm, "end": v(33, 90) * mm});
            skLineSegment(sketch, "E87", {"start": v(-80, 0) * mm, "end": v(80, 0) * mm, "construction": true});
            skLineSegment(sketch, "E88.MirrorCS", {"start": v(33, 90) * mm, "end": v(-33, 90) * mm});
            skArc(sketch, "E89.MirrorCS", {"start": v(-15, 120) * mm, "mid": v(0, 135) * mm, "end": v(15, 120) * mm});
            skLineSegment(sketch, "E90.MirrorCS", {"start": v(80, 0) * mm, "end": v(-80, 0) * mm, "construction": true});
            skLineSegment(sketch, "E91.MirrorCS", {"start": v(15, -120) * mm, "end": v(15, -108) * mm});
            skArc(sketch, "E92.MirrorCS", {"start": v(-15, -120) * mm, "mid": v(0, -135) * mm, "end": v(15, -120) * mm});
            skCircle(sketch, "E93.MirrorC", {"center": v(0, -120) * mm, "radius": 6 * mm});
            skLineSegment(sketch, "E94.MirrorCS", {"start": v(15, -108) * mm, "end": v(33, -90) * mm});
            skLineSegment(sketch, "E95.MirrorCS", {"start": v(-15, -108) * mm, "end": v(-33, -90) * mm});
            skLineSegment(sketch, "E96.MirrorCS", {"start": v(-15, -120) * mm, "end": v(-15, -108) * mm});
            skLineSegment(sketch, "E97.MirrorCS", {"start": v(33, -90) * mm, "end": v(-33, -90) * mm});
            skLineSegment(sketch, "E98.MirrorCS", {"start": v(-33, -90) * mm, "end": v(33, -90) * mm});
            skArc(sketch, "E99.MirrorCS", {"start": v(15, -120) * mm, "mid": v(0, -135) * mm, "end": v(-15, -120) * mm});
            skLineSegment(sketch, "E100.MirrorCS", {"start": v(0, -90) * mm, "end": v(0, -120) * mm, "construction": true});
            skSolve(sketch);
        }
        {
            var Q0;
            Q0 = qSketchRegion(id + "F16", true);
            var Q1;
            {var subQ4=sQuery(id+"F16.wireOp",EDGE,"E85");Q1=makeQuery(id+"F16.imprint","IMPRINT",FACE,{"disambiguationData":[TD([[makeQuery(id+"F16.imprint","IMPRINT",EDGE,{"derivedFrom":subQ4}),-1.0]])]});}
            var Q2;
            Q2=makeQuery(id+"F2.opExtrude","CAP_FACE",FACE,{"disambiguationData":[OSD([sQuery(id+"F0.wireOp",EDGE,"E12"),sQuery(id+"F0.wireOp",EDGE,"E13"),sQuery(id+"F0.wireOp",EDGE,"E14"),sQuery(id+"F0.wireOp",EDGE,"E15"),sQuery(id+"F0.wireOp",EDGE,"E17.filletArc"),sQuery(id+"F0.wireOp",EDGE,"E18.filletArc"),sQuery(id+"F0.wireOp",EDGE,"E19.filletArc"),sQuery(id+"F0.wireOp",EDGE,"E20.filletArc"),sQuery(id+"F0.wireOp",EDGE,"E25.0"),sQuery(id+"F0.wireOp",EDGE,"E25.1"),sQuery(id+"F0.wireOp",EDGE,"E25.2"),sQuery(id+"F0.wireOp",EDGE,"E25.3"),sQuery(id+"F0.wireOp",EDGE,"E25.4"),sQuery(id+"F0.wireOp",EDGE,"E25.5"),sQuery(id+"F0.wireOp",EDGE,"E25.6"),sQuery(id+"F0.wireOp",EDGE,"E25.7")])],"isStart":false});
            extrude(context, id + "F17", {"entities" : qUnion([Q0, Q1]), "endBound" : BoundingType.UP_TO_SURFACE, "depth" : 25 * mm, "endBoundEntityFace" : qUnion([Q2]), "offsetDistance" : 25 * mm});
        }
    });
